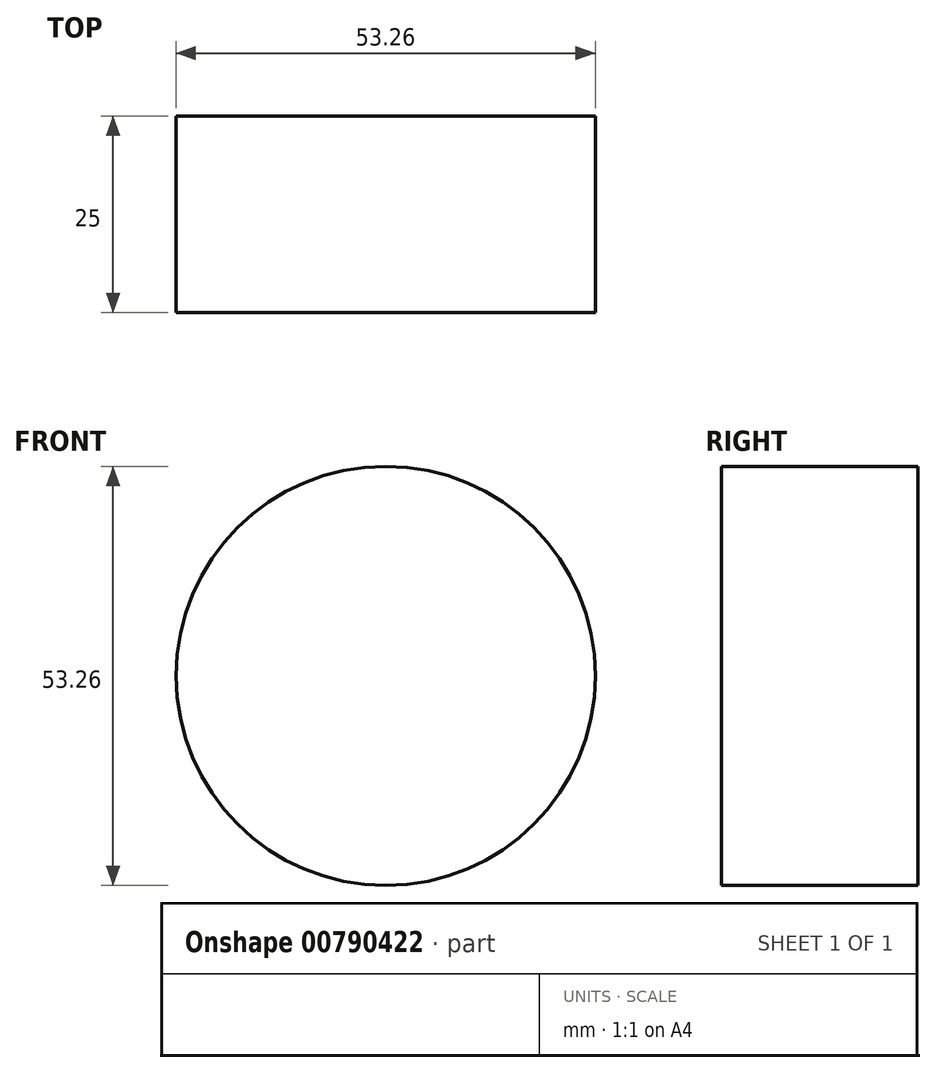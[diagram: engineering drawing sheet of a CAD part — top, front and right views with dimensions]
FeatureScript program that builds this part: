
annotation { "Feature Type Name" : "Feature", "Feature Type Description" : "" }
export const myFeature = defineFeature(function(context is Context, id is Id, definition is map)
    precondition{}
    {
        {
            var Q0;
            Q0=qCreatedBy(makeId("Front.planeOp"),FACE);
            var sketch = newSketch(context, id + "F0", { "sketchPlane" : qUnion([Q0])});
            skCircle(sketch, "E0", {"center": v(0, 0) * mm, "radius": 30.98 * mm});
            skCircle(sketch, "E1", {"center": v(0, 0) * mm, "radius": 26.63 * mm});
            skSolve(sketch);
        }
        {
            var Q0;
            Q0=makeQuery(id+"F0.imprint","IMPRINT",FACE,{"disambiguationData":[TD([[makeQuery(id+"F0.imprint","IMPRINT",EDGE,{"derivedFrom":sQuery(id+"F0.wireOp",EDGE,"E1")}),1.0]])]});
            extrude(context, id + "F1", {"entities" : qUnion([Q0]), "depth" : 25 * mm, "offsetDistance" : 25 * mm});
        }
        {
            var Q0;
            Q0=sQuery(id+"F0.wireOp",EDGE,"E1");
            var Q1;
            Q1=sQuery(id+"F0.wireOp",EDGE,"E0");
            extrude(context, id + "F2", {"bodyType" : ToolBodyType.SURFACE, "surfaceEntities" : qUnion([Q0, Q1]), "depth" : 25 * mm, "offsetDistance" : 25 * mm});
        }
    });
